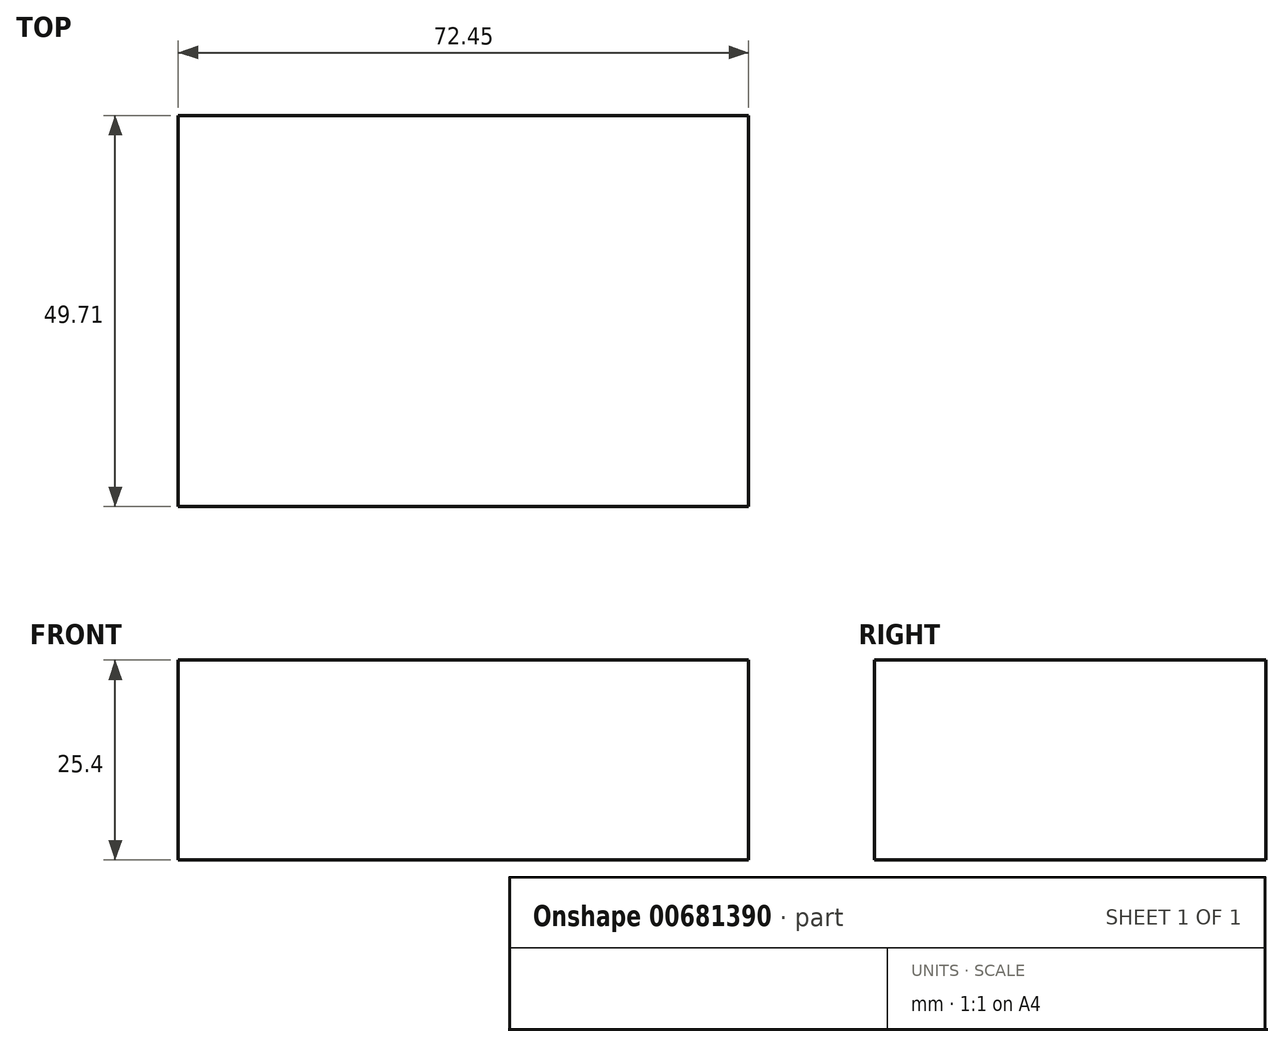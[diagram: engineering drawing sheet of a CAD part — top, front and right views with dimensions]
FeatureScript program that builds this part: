
annotation { "Feature Type Name" : "Feature", "Feature Type Description" : "" }
export const myFeature = defineFeature(function(context is Context, id is Id, definition is map)
    precondition{}
    {
        {
            var Q0;
            Q0=qCreatedBy(makeId("Top.planeOp"),FACE);
            var sketch = newSketch(context, id + "F0", { "sketchPlane" : qUnion([Q0])});
            skLineSegment(sketch, "E0.bottom", {"start": v(0, 0) * mm, "end": v(-72.45, 0) * mm});
            skLineSegment(sketch, "E0.top", {"start": v(0, 49.7) * mm, "end": v(-72.45, 49.7) * mm});
            skLineSegment(sketch, "E0.left", {"start": v(0, 0) * mm, "end": v(0, 49.7) * mm});
            skLineSegment(sketch, "E0.right", {"start": v(-72.45, 0) * mm, "end": v(-72.45, 49.7) * mm});
            skSolve(sketch);
        }
        {
            var Q0;
            Q0=makeQuery(id+"F0.imprint","IMPRINT",FACE,{"disambiguationData":[TD([[makeQuery(id+"F0.imprint","IMPRINT",EDGE,{"derivedFrom":sQuery(id+"F0.wireOp",EDGE,"E0.bottom")}),-1.0]])]});
            extrude(context, id + "F1", {"entities" : qUnion([Q0]), "depth" : 25.4 * mm, "offsetDistance" : 25.4 * mm});
        }
    });
